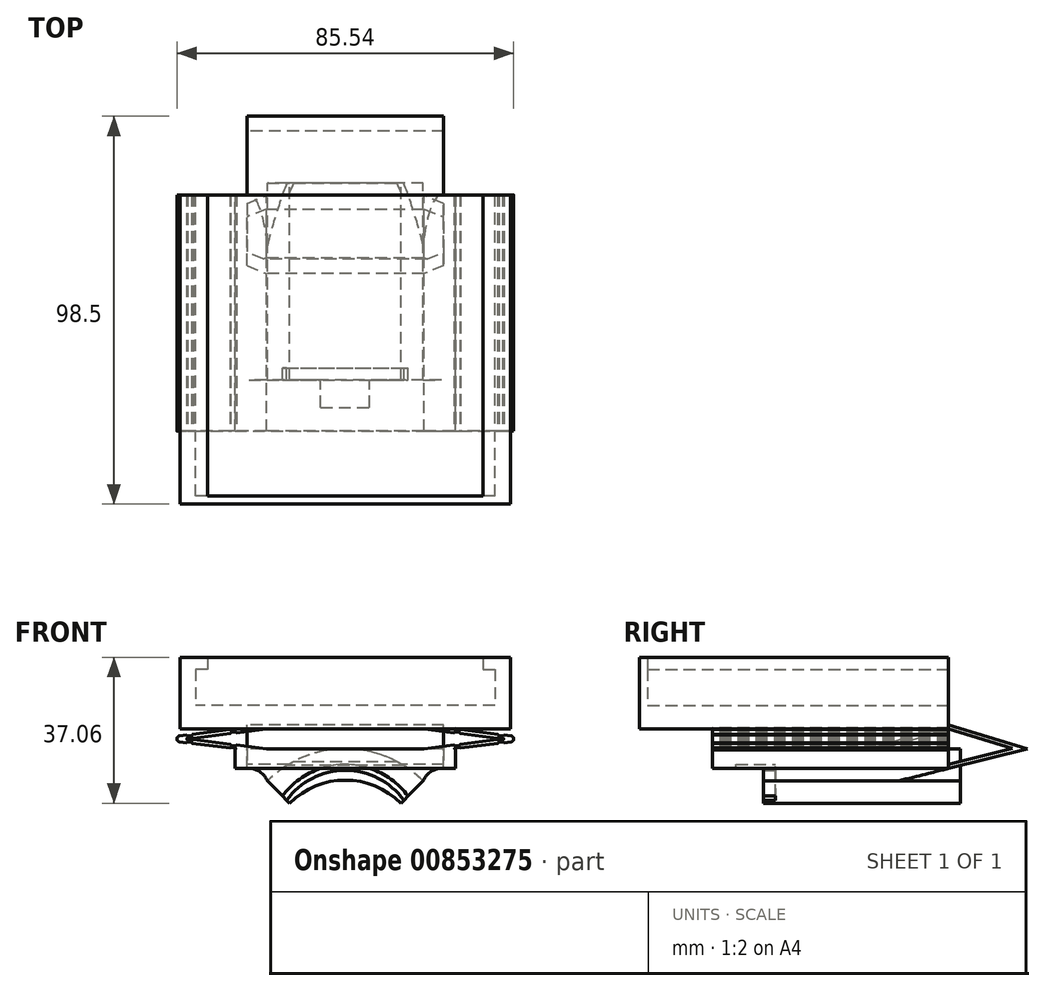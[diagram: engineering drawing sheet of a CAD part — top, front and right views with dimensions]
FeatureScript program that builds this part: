
annotation { "Feature Type Name" : "Feature", "Feature Type Description" : "" }
export const myFeature = defineFeature(function(context is Context, id is Id, definition is map)
    precondition{}
    {
        {
            var Q0;
            Q0=qCreatedBy(makeId("Front.planeOp"),FACE);
            var sketch = newSketch(context, id + "F0", { "sketchPlane" : qUnion([Q0])});
            skLineSegment(sketch, "E0", {"start": v(-35, 12.2) * mm, "end": v(-35, 9.2) * mm});
            skLineSegment(sketch, "E1", {"start": v(-35, 9.2) * mm, "end": v(-38, 9.2) * mm});
            skLineSegment(sketch, "E2", {"start": v(-38, 0) * mm, "end": v(0, 0) * mm});
            skLineSegment(sketch, "E3", {"start": v(-35, 12.2) * mm, "end": v(-42, 12.2) * mm});
            skLineSegment(sketch, "E4", {"start": v(-42, 12.2) * mm, "end": v(-42, -6) * mm});
            skLineSegment(sketch, "E5", {"start": v(-38, 9.2) * mm, "end": v(-38, 0) * mm});
            skLineSegment(sketch, "E6", {"start": v(-42, -6) * mm, "end": v(0, -6) * mm});
            skLineSegment(sketch, "E7.MirrorCS", {"start": v(35, 12.2) * mm, "end": v(35, 9.2) * mm});
            skLineSegment(sketch, "E8.MirrorCS", {"start": v(35, 9.2) * mm, "end": v(38, 9.2) * mm});
            skLineSegment(sketch, "E9.MirrorCS", {"start": v(35, 12.2) * mm, "end": v(42, 12.2) * mm});
            skLineSegment(sketch, "E10.MirrorCS", {"start": v(38, 9.2) * mm, "end": v(38, 0) * mm});
            skLineSegment(sketch, "E11.MirrorCS", {"start": v(42, -6) * mm, "end": v(0, -6) * mm});
            skLineSegment(sketch, "E12.MirrorCS", {"start": v(38, 0) * mm, "end": v(0, 0) * mm});
            skLineSegment(sketch, "E13.MirrorCS", {"start": v(42, 12.2) * mm, "end": v(42, -6) * mm});
            skSolve(sketch);
        }
        {
            var Q0;
            Q0 = qSketchRegion(id + "F0", true);
            extrude(context, id + "F1", {"entities" : qUnion([Q0]), "depth" : 76.5 * mm, "offsetDistance" : 25.4 * mm});
        }
        {
            var Q0;
            Q0=qCreatedBy(makeId("Front.planeOp"),FACE);
            var sketch = newSketch(context, id + "F2", { "sketchPlane" : qUnion([Q0])});
            skLineSegment(sketch, "E14", {"start": v(-20, -6) * mm, "end": v(-40, -8.5) * mm});
            skLineSegment(sketch, "E15", {"start": v(-40, -8.5) * mm, "end": v(-20, -11) * mm});
            skLineSegment(sketch, "E16", {"start": v(-20, -6) * mm, "end": v(-28.06, -6) * mm});
            skLineSegment(sketch, "E17", {"start": v(-28.06, -6) * mm, "end": v(-48.06, -8.5) * mm});
            skLineSegment(sketch, "E18", {"start": v(-48.06, -8.5) * mm, "end": v(-28.06, -11) * mm});
            skLineSegment(sketch, "E19", {"start": v(-28.06, -11) * mm, "end": v(-28.06, -16) * mm});
            skLineSegment(sketch, "E20", {"start": v(-28.06, -16) * mm, "end": v(0, -16) * mm});
            skLineSegment(sketch, "E21", {"start": v(-20, -11) * mm, "end": v(0, -11) * mm});
            skLineSegment(sketch, "E22.MirrorCS", {"start": v(28.06, -11) * mm, "end": v(28.06, -16) * mm});
            skLineSegment(sketch, "E23.MirrorCS", {"start": v(20, -6) * mm, "end": v(28.06, -6) * mm});
            skLineSegment(sketch, "E24.MirrorCS", {"start": v(20, -6) * mm, "end": v(40, -8.5) * mm});
            skLineSegment(sketch, "E25.MirrorCS", {"start": v(48.06, -8.5) * mm, "end": v(28.06, -11) * mm});
            skLineSegment(sketch, "E26.MirrorCS", {"start": v(40, -8.5) * mm, "end": v(20, -11) * mm});
            skLineSegment(sketch, "E27.MirrorCS", {"start": v(20, -11) * mm, "end": v(0, -11) * mm});
            skLineSegment(sketch, "E28.MirrorCS", {"start": v(28.06, -6) * mm, "end": v(48.06, -8.5) * mm});
            skLineSegment(sketch, "E29.MirrorCS", {"start": v(28.06, -16) * mm, "end": v(0, -16) * mm});
            skSolve(sketch);
        }
        {
            var Q0;
            Q0 = qSketchRegion(id + "F2", true);
            extrude(context, id + "F3", {"entities" : qUnion([Q0]), "operationType" : NewBodyOperationType.ADD, "depth" : 60 * mm, "offsetDistance" : 25.4 * mm});
        }
        {
            var Q0;
            Q0=makeQuery(id+"F1.opExtrude","SWEPT_FACE",FACE,{"disambiguationData":[OSD([sQuery(id+"F0.wireOp",EDGE,"E2"),sQuery(id+"F0.wireOp",EDGE,"E12.MirrorCS")])]});
            var sketch = newSketch(context, id + "F4", { "sketchPlane" : qUnion([Q0])});
            skLineSegment(sketch, "E30.bottom", {"start": v(-42, -78.5) * mm, "end": v(42, -78.5) * mm});
            skLineSegment(sketch, "E30.top", {"start": v(-42, -76.5) * mm, "end": v(42, -76.5) * mm});
            skLineSegment(sketch, "E30.left", {"start": v(-42, -76.5) * mm, "end": v(-42, -78.5) * mm});
            skLineSegment(sketch, "E31", {"start": v(42, -76.5) * mm, "end": v(42, -78.5) * mm});
            skSolve(sketch);
        }
        {
            var Q0;
            Q0 = qSketchRegion(id + "F4", true);
            var Q1;
            Q1=makeQuery(id+"F1.opExtrude","SWEPT_FACE",FACE,{"disambiguationData":[OSD([sQuery(id+"F0.wireOp",EDGE,"E3")])]});
            var Q2;
            Q2=makeQuery(id+"F1.opExtrude","SWEPT_FACE",FACE,{"disambiguationData":[OSD([sQuery(id+"F0.wireOp",EDGE,"E6"),sQuery(id+"F0.wireOp",EDGE,"E11.MirrorCS")])]});
            extrude(context, id + "F5", {"entities" : qUnion([Q0]), "operationType" : NewBodyOperationType.ADD, "endBound" : BoundingType.UP_TO_SURFACE, "depth" : 25 * mm, "endBoundEntityFace" : qUnion([Q1]), "offsetDistance" : 25 * mm, "hasSecondDirection" : true, "secondDirectionBound" : SecondDirectionBoundingType.UP_TO_SURFACE, "secondDirectionOppositeDirection" : true, "secondDirectionDepth" : 25 * mm, "secondDirectionBoundEntityFace" : qUnion([Q2])});
        }
        {
            var Q0;
            Q0=qCreatedBy(makeId("Right.planeOp"),FACE);
            var sketch = newSketch(context, id + "F6", { "sketchPlane" : qUnion([Q0])});
            skLineSegment(sketch, "E32", {"start": v(0, -16) * mm, "end": v(20, -11) * mm});
            skLineSegment(sketch, "E33", {"start": v(20, -11) * mm, "end": v(0, -4.92) * mm});
            skLineSegment(sketch, "E34", {"start": v(0, -5.97) * mm, "end": v(16.25, -10.9) * mm});
            skLineSegment(sketch, "E35", {"start": v(16.25, -10.9) * mm, "end": v(0, -14.97) * mm});
            skLineSegment(sketch, "E36", {"start": v(0, -4.92) * mm, "end": v(0, -5.97) * mm});
            skLineSegment(sketch, "E37", {"start": v(0, -16) * mm, "end": v(0, -14.97) * mm});
            skLineSegment(sketch, "E38.MirrorCS", {"start": v(0, -5.97) * mm, "end": v(-16.25, -10.9) * mm});
            skLineSegment(sketch, "E39.MirrorCS", {"start": v(0, -16) * mm, "end": v(-20, -11) * mm});
            skLineSegment(sketch, "E40.MirrorCS", {"start": v(-16.25, -10.9) * mm, "end": v(0, -14.97) * mm});
            skLineSegment(sketch, "E41.MirrorCS", {"start": v(-20, -11) * mm, "end": v(0, -4.92) * mm});
            skSolve(sketch);
        }
        {
            var Q0;
            Q0 = qSketchRegion(id + "F6", true);
            extrude(context, id + "F7", {"entities" : qUnion([Q0]), "operationType" : NewBodyOperationType.ADD, "depth" : 25 * mm, "offsetDistance" : 25 * mm, "hasSecondDirection" : true, "secondDirectionOppositeDirection" : true, "secondDirectionDepth" : 25 * mm});
        }
        {
            var Q0;
            Q0=qCreatedBy(makeId("Right.planeOp"),FACE);
            var sketch = newSketch(context, id + "F8", { "sketchPlane" : qUnion([Q0])});
            skLineSegment(sketch, "E42.bottom", {"start": v(-47, -11) * mm, "end": v(3, -11) * mm});
            skLineSegment(sketch, "E42.top", {"start": v(-47, -19) * mm, "end": v(3, -19) * mm});
            skLineSegment(sketch, "E42.left", {"start": v(3, -11) * mm, "end": v(3, -19) * mm});
            skLineSegment(sketch, "E42.right", {"start": v(-47, -11) * mm, "end": v(-47, -19) * mm});
            skLineSegment(sketch, "E43", {"start": v(-47, -39) * mm, "end": v(3, -39) * mm});
            skSolve(sketch);
        }
        {
            var Q0;
            Q0 = qSketchRegion(id + "F8", true);
            var Q1;
            Q1=sQuery(id+"F8.wireOp",EDGE,"E43");
            revolve(context, id + "F9", {"operationType" : NewBodyOperationType.ADD, "surfaceOperationType" : NewSurfaceOperationType.NEW, "entities" : qUnion([Q0]), "axis" : qUnion([Q1]), "revolveType" : RevolveType.SYMMETRIC, "angle" : 90 * degree});
        }
        {
            var Q0;
            Q0=makeQuery(id+"F9.boolean.opBoolean","INTERSECT",EDGE,{"disambiguationData":[OD(1.0)],"derivedFrom":[makeQuery(id+"F3.opExtrude","SWEPT_FACE",FACE,{"disambiguationData":[OSD([sQuery(id+"F2.wireOp",EDGE,"E20"),sQuery(id+"F2.wireOp",EDGE,"E29.MirrorCS")])]}),makeQuery(id+"F9.opRevolve","SWEPT_FACE",FACE,{"disambiguationData":[OSD([sQuery(id+"F8.wireOp",EDGE,"E42.bottom")])]})]});
            var Q1;
            Q1=makeQuery(id+"F9.boolean.opBoolean","INTERSECT",EDGE,{"disambiguationData":[OD(0.0)],"derivedFrom":[makeQuery(id+"F3.opExtrude","SWEPT_FACE",FACE,{"disambiguationData":[OSD([sQuery(id+"F2.wireOp",EDGE,"E20"),sQuery(id+"F2.wireOp",EDGE,"E29.MirrorCS")])]}),makeQuery(id+"F9.opRevolve","SWEPT_FACE",FACE,{"disambiguationData":[OSD([sQuery(id+"F8.wireOp",EDGE,"E42.bottom")])]})]});
            fillet(context, id + "F10", {"entities" : qUnion([Q0, Q1]), "radius" : 5 * mm, "tangentPropagation" : true, "allowEdgeOverflow" : false});
        }
        {
            var Q0;
            Q0=qCreatedBy(makeId("Right.planeOp"),FACE);
            var sketch = newSketch(context, id + "F11", { "sketchPlane" : qUnion([Q0])});
            skLineSegment(sketch, "E44.bottom", {"start": v(-54, -15) * mm, "end": v(-49, -15) * mm});
            skLineSegment(sketch, "E44.top", {"start": v(-54, -16.5) * mm, "end": v(-49, -16.5) * mm});
            skLineSegment(sketch, "E44.left", {"start": v(-54, -15) * mm, "end": v(-54, -16.5) * mm});
            skLineSegment(sketch, "E44.right", {"start": v(-49, -15) * mm, "end": v(-49, -16.5) * mm});
            skLineSegment(sketch, "E45.bottom", {"start": v(-49, -15) * mm, "end": v(-44, -15) * mm});
            skLineSegment(sketch, "E45.top", {"start": v(-49, -16.5) * mm, "end": v(-44, -16.5) * mm});
            skLineSegment(sketch, "E45.right", {"start": v(-44, -16.5) * mm, "end": v(-44, -15) * mm});
            skLineSegment(sketch, "E46", {"start": v(-47, -34.86) * mm, "end": v(3, -34.86) * mm});
            skSolve(sketch);
        }
        {
            var Q0;
            Q0 = qSketchRegion(id + "F11", true);
            var Q1;
            Q1=sQuery(id+"F11.wireOp",EDGE,"E46");
            revolve(context, id + "F12", {"operationType" : NewBodyOperationType.REMOVE, "surfaceOperationType" : NewSurfaceOperationType.NEW, "entities" : qUnion([Q0]), "axis" : qUnion([Q1]), "revolveType" : RevolveType.FULL, "oppositeDirection" : true});
        }
        {
            var Q0;
            Q0=makeQuery(id+"F3.opExtrude","CAP_FACE",FACE,{"disambiguationData":[OSD([sQuery(id+"F2.wireOp",EDGE,"E14"),sQuery(id+"F2.wireOp",EDGE,"E15"),sQuery(id+"F2.wireOp",EDGE,"E16"),sQuery(id+"F2.wireOp",EDGE,"E17"),sQuery(id+"F2.wireOp",EDGE,"E18"),sQuery(id+"F2.wireOp",EDGE,"E19"),sQuery(id+"F2.wireOp",EDGE,"E20"),sQuery(id+"F2.wireOp",EDGE,"E21"),sQuery(id+"F2.wireOp",EDGE,"E22.MirrorCS"),sQuery(id+"F2.wireOp",EDGE,"E23.MirrorCS"),sQuery(id+"F2.wireOp",EDGE,"E24.MirrorCS"),sQuery(id+"F2.wireOp",EDGE,"E25.MirrorCS"),sQuery(id+"F2.wireOp",EDGE,"E26.MirrorCS"),sQuery(id+"F2.wireOp",EDGE,"E27.MirrorCS"),sQuery(id+"F2.wireOp",EDGE,"E28.MirrorCS"),sQuery(id+"F2.wireOp",EDGE,"E29.MirrorCS")])],"isStart":false});
            var sketch = newSketch(context, id + "F13", { "sketchPlane" : qUnion([Q0])});
            skArc(sketch, "E47", {"start": v(40, -8.75) * mm, "mid": v(40.25, -8.5) * mm, "end": v(40, -8.25) * mm});
            skArc(sketch, "E48", {"start": v(40.06, -7.75) * mm, "mid": v(40.34, -7.53) * mm, "end": v(40.12, -7.26) * mm});
            skArc(sketch, "E49", {"start": v(28.06, -5.75) * mm, "mid": v(27.81, -5.97) * mm, "end": v(28, -6.24) * mm});
            skArc(sketch, "E50", {"start": v(39.13, -7.13) * mm, "mid": v(38.85, -7.35) * mm, "end": v(39.07, -7.63) * mm});
            skArc(sketch, "E51", {"start": v(39, -8.13) * mm, "mid": v(38.8, -8.16) * mm, "end": v(38.7, -8.34) * mm});
            skArc(sketch, "E52", {"start": v(38.67, -8.6) * mm, "mid": v(38.74, -8.81) * mm, "end": v(38.95, -8.88) * mm});
            skArc(sketch, "E53", {"start": v(27.94, -6.74) * mm, "mid": v(27.66, -6.96) * mm, "end": v(27.88, -7.24) * mm});
            skArc(sketch, "E54", {"start": v(28.93, -6.86) * mm, "mid": v(29.15, -7.14) * mm, "end": v(28.87, -7.36) * mm});
            skLineSegment(sketch, "E55", {"start": v(28, -6.24) * mm, "end": v(29, -6.37) * mm});
            skLineSegment(sketch, "E56", {"start": v(39, -8.13) * mm, "end": v(40, -8.25) * mm});
            skLineSegment(sketch, "E57", {"start": v(40, -8.75) * mm, "end": v(38.95, -8.88) * mm});
            skLineSegment(sketch, "E58", {"start": v(27.94, -6.74) * mm, "end": v(28.93, -6.86) * mm});
            skLineSegment(sketch, "E59", {"start": v(28.06, -5.75) * mm, "end": v(29.05, -5.87) * mm});
            skLineSegment(sketch, "E60", {"start": v(39.07, -7.63) * mm, "end": v(40.06, -7.75) * mm});
            skLineSegment(sketch, "E61", {"start": v(39.13, -7.13) * mm, "end": v(40.12, -7.26) * mm});
            skLineSegment(sketch, "E62", {"start": v(27.88, -7.24) * mm, "end": v(28.87, -7.36) * mm});
            skArc(sketch, "E63", {"start": v(29.05, -5.87) * mm, "mid": v(29.27, -6.15) * mm, "end": v(29, -6.37) * mm});
            skLineSegment(sketch, "E64", {"start": v(38.7, -8.34) * mm, "end": v(38.67, -8.6) * mm});
            skLineSegment(sketch, "E65", {"start": v(29, -6.37) * mm, "end": v(28.93, -6.86) * mm, "construction": true});
            skLineSegment(sketch, "E66", {"start": v(40.06, -7.75) * mm, "end": v(40, -8.25) * mm, "construction": true});
            skLineSegment(sketch, "E67", {"start": v(40, -8.5) * mm, "end": v(36.43, -8.5) * mm, "construction": true});
            skLineSegment(sketch, "E68.MirrorCS", {"start": v(39.13, -9.87) * mm, "end": v(40.12, -9.74) * mm});
            skLineSegment(sketch, "E69.MirrorCS", {"start": v(39.07, -9.37) * mm, "end": v(40.06, -9.25) * mm});
            skArc(sketch, "E70.MirrorCS", {"start": v(39.13, -9.87) * mm, "mid": v(38.85, -9.65) * mm, "end": v(39.07, -9.37) * mm});
            skArc(sketch, "E71.MirrorCS", {"start": v(40.06, -9.25) * mm, "mid": v(40.34, -9.47) * mm, "end": v(40.12, -9.74) * mm});
            skLineSegment(sketch, "E72.MirrorCS", {"start": v(29, -10.63) * mm, "end": v(28.93, -10.14) * mm, "construction": true});
            skArc(sketch, "E73.MirrorCS", {"start": v(28.93, -10.14) * mm, "mid": v(29.15, -9.86) * mm, "end": v(28.87, -9.64) * mm});
            skArc(sketch, "E74.MirrorCS", {"start": v(27.94, -10.26) * mm, "mid": v(27.66, -10.04) * mm, "end": v(27.88, -9.76) * mm});
            skArc(sketch, "E75.MirrorCS", {"start": v(28.06, -11.25) * mm, "mid": v(27.81, -11.03) * mm, "end": v(28, -10.76) * mm});
            skArc(sketch, "E76.MirrorCS", {"start": v(29.05, -11.13) * mm, "mid": v(29.27, -10.85) * mm, "end": v(29, -10.63) * mm});
            skLineSegment(sketch, "E77.MirrorCS", {"start": v(28, -10.76) * mm, "end": v(29, -10.63) * mm});
            skLineSegment(sketch, "E78.MirrorCS", {"start": v(27.94, -10.26) * mm, "end": v(28.93, -10.14) * mm});
            skLineSegment(sketch, "E79.MirrorCS", {"start": v(27.88, -9.76) * mm, "end": v(28.87, -9.64) * mm});
            skLineSegment(sketch, "E80.MirrorCS", {"start": v(28.06, -11.25) * mm, "end": v(29.05, -11.13) * mm});
            skLineSegment(sketch, "E81", {"start": v(0, 0) * mm, "end": v(0, -38.54) * mm, "construction": true});
            skLineSegment(sketch, "E82.MirrorCS", {"start": v(-38.7, -8.34) * mm, "end": v(-38.67, -8.6) * mm});
            skLineSegment(sketch, "E83.MirrorCS", {"start": v(-39.07, -7.63) * mm, "end": v(-40.06, -7.75) * mm});
            skLineSegment(sketch, "E84.MirrorCS", {"start": v(-39, -8.13) * mm, "end": v(-40, -8.25) * mm});
            skLineSegment(sketch, "E85.MirrorCS", {"start": v(-39.07, -9.37) * mm, "end": v(-40.06, -9.25) * mm});
            skLineSegment(sketch, "E86.MirrorCS", {"start": v(-40, -8.75) * mm, "end": v(-38.95, -8.88) * mm});
            skArc(sketch, "E87.MirrorCS", {"start": v(-39.13, -7.13) * mm, "mid": v(-38.85, -7.35) * mm, "end": v(-39.07, -7.63) * mm});
            skLineSegment(sketch, "E88.MirrorCS", {"start": v(-28.06, -5.75) * mm, "end": v(-29.05, -5.87) * mm});
            skLineSegment(sketch, "E89.MirrorCS", {"start": v(-27.88, -9.76) * mm, "end": v(-28.87, -9.64) * mm});
            skLineSegment(sketch, "E90.MirrorCS", {"start": v(-28, -10.76) * mm, "end": v(-29, -10.63) * mm});
            skLineSegment(sketch, "E91.MirrorCS", {"start": v(-28, -6.24) * mm, "end": v(-29, -6.37) * mm});
            skArc(sketch, "E92.MirrorCS", {"start": v(-40.06, -7.75) * mm, "mid": v(-40.34, -7.53) * mm, "end": v(-40.12, -7.26) * mm});
            skArc(sketch, "E93.MirrorCS", {"start": v(-39, -8.13) * mm, "mid": v(-38.8, -8.16) * mm, "end": v(-38.7, -8.34) * mm});
            skArc(sketch, "E94.MirrorCS", {"start": v(-38.67, -8.6) * mm, "mid": v(-38.74, -8.81) * mm, "end": v(-38.95, -8.88) * mm});
            skArc(sketch, "E95.MirrorCS", {"start": v(-40, -8.75) * mm, "mid": v(-40.25, -8.5) * mm, "end": v(-40, -8.25) * mm});
            skArc(sketch, "E96.MirrorCS", {"start": v(-40.06, -9.25) * mm, "mid": v(-40.34, -9.47) * mm, "end": v(-40.12, -9.74) * mm});
            skLineSegment(sketch, "E97.MirrorCS", {"start": v(-39.13, -7.13) * mm, "end": v(-40.12, -7.26) * mm});
            skLineSegment(sketch, "E98.MirrorCS", {"start": v(-27.94, -6.74) * mm, "end": v(-28.93, -6.86) * mm});
            skLineSegment(sketch, "E99.MirrorCS", {"start": v(-40.06, -7.75) * mm, "end": v(-40, -8.25) * mm, "construction": true});
            skArc(sketch, "E100.MirrorCS", {"start": v(-39.13, -9.87) * mm, "mid": v(-38.85, -9.65) * mm, "end": v(-39.07, -9.37) * mm});
            skLineSegment(sketch, "E101.MirrorCS", {"start": v(-39.13, -9.87) * mm, "end": v(-40.12, -9.74) * mm});
            skLineSegment(sketch, "E102.MirrorCS", {"start": v(-27.94, -10.26) * mm, "end": v(-28.93, -10.14) * mm});
            skArc(sketch, "E103.MirrorCS", {"start": v(-28.06, -11.25) * mm, "mid": v(-27.81, -11.03) * mm, "end": v(-28, -10.76) * mm});
            skArc(sketch, "E104.MirrorCS", {"start": v(-29.05, -11.13) * mm, "mid": v(-29.27, -10.85) * mm, "end": v(-29, -10.63) * mm});
            skArc(sketch, "E105.MirrorCS", {"start": v(-28.93, -10.14) * mm, "mid": v(-29.15, -9.86) * mm, "end": v(-28.87, -9.64) * mm});
            skArc(sketch, "E106.MirrorCS", {"start": v(-29.05, -5.87) * mm, "mid": v(-29.27, -6.15) * mm, "end": v(-29, -6.37) * mm});
            skArc(sketch, "E107.MirrorCS", {"start": v(-28.06, -5.75) * mm, "mid": v(-27.81, -5.97) * mm, "end": v(-28, -6.24) * mm});
            skArc(sketch, "E108.MirrorCS", {"start": v(-27.94, -6.74) * mm, "mid": v(-27.66, -6.96) * mm, "end": v(-27.88, -7.24) * mm});
            skArc(sketch, "E109.MirrorCS", {"start": v(-27.94, -10.26) * mm, "mid": v(-27.66, -10.04) * mm, "end": v(-27.88, -9.76) * mm});
            skLineSegment(sketch, "E110.MirrorCS", {"start": v(-29, -10.63) * mm, "end": v(-28.93, -10.14) * mm, "construction": true});
            skLineSegment(sketch, "E111.MirrorCS", {"start": v(-27.88, -7.24) * mm, "end": v(-28.87, -7.36) * mm});
            skArc(sketch, "E112.MirrorCS", {"start": v(-28.93, -6.86) * mm, "mid": v(-29.15, -7.14) * mm, "end": v(-28.87, -7.36) * mm});
            skLineSegment(sketch, "E113.MirrorCS", {"start": v(-40, -8.5) * mm, "end": v(-36.43, -8.5) * mm, "construction": true});
            skLineSegment(sketch, "E114.MirrorCS", {"start": v(-29, -6.37) * mm, "end": v(-28.93, -6.86) * mm, "construction": true});
            skLineSegment(sketch, "E115.MirrorCS", {"start": v(-28.06, -11.25) * mm, "end": v(-29.05, -11.13) * mm});
            skSolve(sketch);
        }
        {
            var Q0;
            Q0 = qSketchRegion(id + "F13", true);
            var Q1;
            Q1=makeQuery(id+"F3.opExtrude","CAP_FACE",FACE,{"disambiguationData":[OSD([sQuery(id+"F2.wireOp",EDGE,"E14"),sQuery(id+"F2.wireOp",EDGE,"E15"),sQuery(id+"F2.wireOp",EDGE,"E16"),sQuery(id+"F2.wireOp",EDGE,"E17"),sQuery(id+"F2.wireOp",EDGE,"E18"),sQuery(id+"F2.wireOp",EDGE,"E19"),sQuery(id+"F2.wireOp",EDGE,"E20"),sQuery(id+"F2.wireOp",EDGE,"E21"),sQuery(id+"F2.wireOp",EDGE,"E22.MirrorCS"),sQuery(id+"F2.wireOp",EDGE,"E23.MirrorCS"),sQuery(id+"F2.wireOp",EDGE,"E24.MirrorCS"),sQuery(id+"F2.wireOp",EDGE,"E25.MirrorCS"),sQuery(id+"F2.wireOp",EDGE,"E26.MirrorCS"),sQuery(id+"F2.wireOp",EDGE,"E27.MirrorCS"),sQuery(id+"F2.wireOp",EDGE,"E28.MirrorCS"),sQuery(id+"F2.wireOp",EDGE,"E29.MirrorCS")])],"isStart":true});
            extrude(context, id + "F14", {"entities" : qUnion([Q0]), "operationType" : NewBodyOperationType.REMOVE, "endBound" : BoundingType.UP_TO_SURFACE, "oppositeDirection" : true, "depth" : 25 * mm, "endBoundEntityFace" : qUnion([Q1]), "offsetDistance" : 25 * mm});
        }
        {
            var Q0;
            Q0=makeQuery(id+"F3.opExtrude","SWEPT_EDGE",EDGE,{"disambiguationData":[OSD([sQuery(id+"F2.wireOp",EDGE,"E25.MirrorCS"),sQuery(id+"F2.wireOp",EDGE,"E28.MirrorCS")])]});
            var Q1;
            Q1=makeQuery(id+"F3.opExtrude","SWEPT_EDGE",EDGE,{"disambiguationData":[OSD([sQuery(id+"F2.wireOp",EDGE,"E17"),sQuery(id+"F2.wireOp",EDGE,"E18")])]});
            fillet(context, id + "F15", {"entities" : qUnion([Q0, Q1]), "radius" : 0.75 * mm, "tangentPropagation" : true, "allowEdgeOverflow" : false});
        }
    });
